# Revit family: TBL4 Steelcase Coalesse - Enea Lottus - Table - Cafe
name_source: partatom
category: Furniture
revit_build: Autodesk Revit 2017 (Build: 20160303_1130(x64)
units: mm (PartAtom-declared; Revit-internal decimal feet)

## family parameters
Always vertical = Yes
Cut with Voids When Loaded = No
Room Calculation Point = No
Shared = No
Work Plane-Based = No

## types (8) — shared parameters
Assembly Code = E2020200
Manufacturer = Steelcase
Product = Enea Lottus
Product Line = Coalesse Seating / Occasional Tables
Release Date = January 2011
URL = http://www.coalesse.com

## per-type parameters (varying)
| type | 24'' W | 30'' W | 36'' W | 42'' W | AutoCAD Tag | Center | Height | Style Number(s) | Width |
| Counter Height - 30" W | No | Yes | No | No | 30/30 | 15.17" | 36.00" | COEL3630 | 30.34" |
| Counter Height - 36" W | No | No | Yes | No | 36/36 | 18.17" | 36.00" | COEL3636 | 36.34" |
| Counter Height - 42" W | No | No | No | Yes | 42/42 | 21.17" | 36.00" | COEL3642 | 42.34" |
| Counter Height - 24" W | Yes | No | No | No | 24/24 | 12.00" | 36.00" | COEL3624 | 24.00" |
| Bar Height - 24" W | Yes | No | No | No | 24/24 | 12.00" | 42.00" | COEL4224 | 24.00" |
| Bar Height - 30" W | No | Yes | No | No | 30/30 | 15.17" | 42.00" | COEL4230 | 30.34" |
| Bar Height - 36" W | No | No | Yes | No | 36/36 | 18.17" | 42.00" | COEL4236 | 36.34" |
| Bar Height - 42" W | No | No | No | Yes | 42/42 | 21.17" | 42.00" | COEL4242 | 42.34" |

## geometry (parser evidence)
native form markers: Sweep x1
no freeform markers — native parametric forms only
